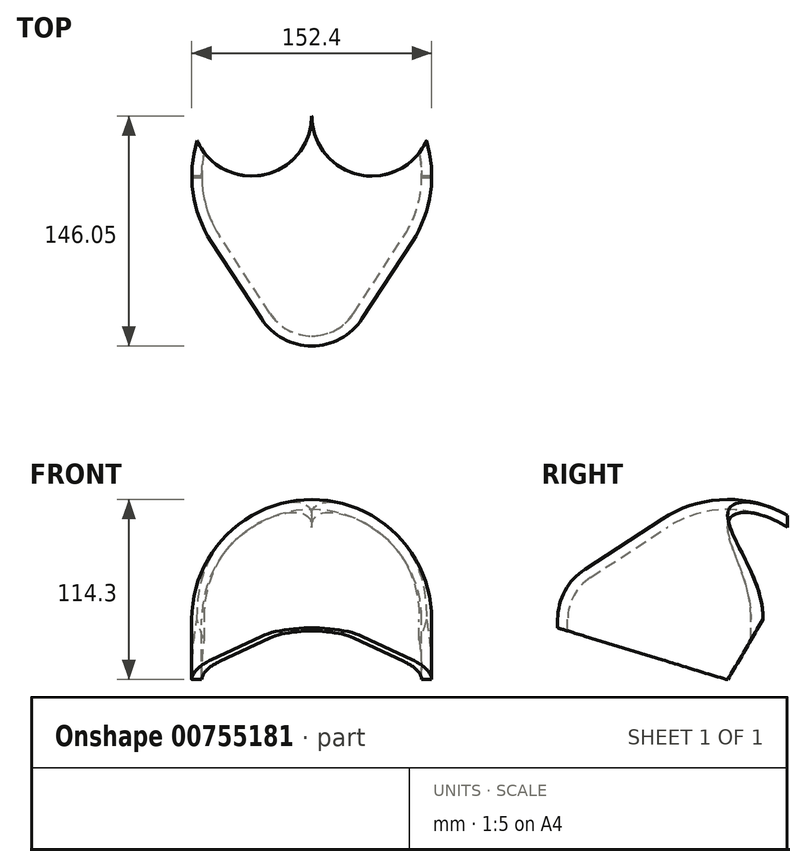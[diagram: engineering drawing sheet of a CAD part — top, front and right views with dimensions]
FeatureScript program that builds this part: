
annotation { "Feature Type Name" : "Feature", "Feature Type Description" : "" }
export const myFeature = defineFeature(function(context is Context, id is Id, definition is map)
    precondition{}
    {
        {
            var Q0;
            Q0=qCreatedBy(makeId("Top.planeOp"),FACE);
            var sketch = newSketch(context, id + "F0", { "sketchPlane" : qUnion([Q0])});
            skLineSegment(sketch, "E0", {"start": v(0, 76.2) * mm, "end": v(0, -101.6) * mm, "construction": true});
            skLineSegment(sketch, "E1", {"start": v(26.61, -87.17) * mm, "end": v(58.54, -38.1) * mm});
            skArc(sketch, "E2.trimOffspring", {"start": v(58.54, -38.1) * mm, "mid": v(61.4, 33.3) * mm, "end": v(0, 69.85) * mm});
            skArc(sketch, "E3.trimOffspring", {"start": v(0, -101.6) * mm, "mid": v(15.14, -97.76) * mm, "end": v(26.61, -87.17) * mm});
            skArc(sketch, "E4.0", {"start": v(63.87, -41.56) * mm, "mid": v(66.98, 36.33) * mm, "end": v(0, 76.2) * mm});
            skLineSegment(sketch, "E4.1", {"start": v(31.93, -90.63) * mm, "end": v(63.87, -41.56) * mm});
            skArc(sketch, "E4.2", {"start": v(0, -107.95) * mm, "mid": v(18.16, -103.34) * mm, "end": v(31.93, -90.63) * mm});
            skLineSegment(sketch, "E5", {"start": v(0, 69.85) * mm, "end": v(0, 76.2) * mm});
            skLineSegment(sketch, "E6", {"start": v(0, -107.95) * mm, "end": v(0, -101.6) * mm});
            skLineSegment(sketch, "E7", {"start": v(-72.03, 0) * mm, "end": v(69.85, 0) * mm, "construction": true});
            skArc(sketch, "E8", {"start": v(0, 38.1) * mm, "mid": v(65.04, 11.16) * mm, "end": v(38.1, 76.2) * mm});
            skArc(sketch, "E9", {"start": v(-38.1, 76.2) * mm, "mid": v(-65.04, 11.16) * mm, "end": v(0, 38.1) * mm});
            skArc(sketch, "E10.trimOffspring", {"start": v(38.1, 76.2) * mm, "mid": v(0, 114.3) * mm, "end": v(-38.1, 76.2) * mm});
            skSolve(sketch);
        }
        {
            var Q0;
            {var subQ0=sQuery(id+"F0.wireOp",EDGE,"E8");var subQ1=sQuery(id+"F0.wireOp",EDGE,"E2.trimOffspring");var subQ2=makeQuery(id+"F0.imprint","INTERSECT",VERTEX,{"disambiguationData":[OD(0.0)],"derivedFrom":[subQ1,subQ0]});Q0=makeQuery(id+"F0.imprint","IMPRINT",FACE,{"disambiguationData":[TD([[makeQuery(id+"F0.imprint","IMPRINT",EDGE,{"disambiguationData":[TD([[subQ2,-1.0]])],"derivedFrom":subQ1}),-1.0]])]});}
            var Q1;
            {var subQ5=sQuery(id+"F0.wireOp",EDGE,"E1");Q1=makeQuery(id+"F0.imprint","IMPRINT",FACE,{"disambiguationData":[TD([[makeQuery(id+"F0.imprint","IMPRINT",EDGE,{"derivedFrom":subQ5}),-1.0]])]});}
            var Q2;
            Q2=sQuery(id+"F0.wireOp",EDGE,"E0");
            revolve(context, id + "F1", {"surfaceOperationType" : NewSurfaceOperationType.NEW, "entities" : qUnion([Q0, Q1]), "axis" : qUnion([Q2]), "revolveType" : RevolveType.ONE_DIRECTION, "angle" : 180 * degree});
        }
        {
            var Q0;
            {var subQ0=sQuery(id+"F0.wireOp",EDGE,"E8");var subQ1=sQuery(id+"F0.wireOp",EDGE,"E4.0");var subQ2=makeQuery(id+"F0.imprint","INTERSECT",VERTEX,{"disambiguationData":[OD(0.0)],"derivedFrom":[subQ1,subQ0]});Q0=makeQuery(id+"F0.imprint","IMPRINT",FACE,{"disambiguationData":[TD([[makeQuery(id+"F0.imprint","IMPRINT",EDGE,{"disambiguationData":[TD([[subQ2,-1.0]])],"derivedFrom":subQ1}),-1.0]])]});}
            var Q1;
            {var subQ0=sQuery(id+"F0.wireOp",EDGE,"E8");var subQ1=sQuery(id+"F0.wireOp",EDGE,"E2.trimOffspring");var subQ2=makeQuery(id+"F0.imprint","INTERSECT",VERTEX,{"disambiguationData":[OD(0.0)],"derivedFrom":[subQ1,subQ0]});Q1=makeQuery(id+"F0.imprint","IMPRINT",FACE,{"disambiguationData":[TD([[makeQuery(id+"F0.imprint","IMPRINT",EDGE,{"disambiguationData":[TD([[subQ2,-1.0]])],"derivedFrom":subQ1}),-1.0]])]});}
            var Q2;
            {var subQ0=sQuery(id+"F0.wireOp",EDGE,"E8");var subQ1=sQuery(id+"F0.wireOp",EDGE,"E2.trimOffspring");var subQ2=makeQuery(id+"F0.imprint","INTERSECT",VERTEX,{"disambiguationData":[OD(0.0)],"derivedFrom":[subQ1,subQ0]});Q2=makeQuery(id+"F0.imprint","IMPRINT",FACE,{"disambiguationData":[TD([[makeQuery(id+"F0.imprint","IMPRINT",EDGE,{"disambiguationData":[TD([[subQ2,-1.0]])],"derivedFrom":subQ1}),1.0]])]});}
            var Q3;
            Q3=makeQuery(id+"F0.imprint","IMPRINT",FACE,{"disambiguationData":[TD([[makeQuery(id+"F0.imprint","IMPRINT",EDGE,{"derivedFrom":sQuery(id+"F0.wireOp",EDGE,"E9")}),1.0]])]});
            var Q4;
            {var subQ0=sQuery(id+"F0.wireOp",EDGE,"3955e8d2-0403-4676-987c-76ff6f28b55b");var subQ1=sQuery(id+"F0.wireOp",EDGE,"E2.trimOffspring");var subQ2=makeQuery(id+"F0.imprint","INTERSECT",VERTEX,{"derivedFrom":[subQ1,subQ0]});Q4=makeQuery(id+"F0.imprint","IMPRINT",FACE,{"disambiguationData":[TD([[makeQuery(id+"F0.imprint","IMPRINT",EDGE,{"disambiguationData":[TD([[subQ2,-1.0]])],"derivedFrom":subQ1}),-1.0]])]});}
            var Q5;
            {var subQ0=sQuery(id+"F0.wireOp",EDGE,"E5");Q5=makeQuery(id+"F0.imprint","IMPRINT",FACE,{"disambiguationData":[TD([[makeQuery(id+"F0.imprint","IMPRINT",EDGE,{"derivedFrom":subQ0}),1.0]])]});}
            extrude(context, id + "F2", {"entities" : qUnion([Q0, Q1, Q2, Q3, Q4, Q5]), "operationType" : NewBodyOperationType.REMOVE, "endBound" : BoundingType.THROUGH_ALL, "depth" : 25.4 * mm, "offsetDistance" : 25.4 * mm});
        }
        {
            var Q0;
            Q0=makeQuery(id+"F1.opRevolve","CAP_FACE",FACE,{"disambiguationData":[OSD([sQuery(id+"F0.wireOp",EDGE,"E1"),sQuery(id+"F0.wireOp",EDGE,"E2.trimOffspring"),sQuery(id+"F0.wireOp",EDGE,"E3.trimOffspring"),sQuery(id+"F0.wireOp",EDGE,"E4.0"),sQuery(id+"F0.wireOp",EDGE,"E4.1"),sQuery(id+"F0.wireOp",EDGE,"E4.2"),sQuery(id+"F0.wireOp",EDGE,"E5"),sQuery(id+"F0.wireOp",EDGE,"E6")])],"isStart":true});
            extrude(context, id + "F3", {"entities" : qUnion([Q0]), "operationType" : NewBodyOperationType.ADD, "depth" : 38.1 * mm, "offsetDistance" : 25.4 * mm});
        }
        {
            var Q0;
            Q0=qCreatedBy(makeId("Right.planeOp"),FACE);
            var sketch = newSketch(context, id + "F4", { "sketchPlane" : qUnion([Q0])});
            skLineSegment(sketch, "E11", {"start": v(111.37, 0) * mm, "end": v(-125.47, 0) * mm, "construction": true});
            skLineSegment(sketch, "E12", {"start": v(0, -74.76) * mm, "end": v(0, 139.83) * mm, "construction": true});
            skLineSegment(sketch, "E13", {"start": v(0, -38.4) * mm, "end": v(22.41, 0) * mm});
            skLineSegment(sketch, "E14", {"start": v(0, -38.4) * mm, "end": v(-125.47, 0) * mm});
            skLineSegment(sketch, "E15", {"start": v(-125.47, -38.4) * mm, "end": v(-125.47, 0) * mm});
            skLineSegment(sketch, "E16", {"start": v(0, -38.4) * mm, "end": v(-125.47, -38.4) * mm});
            skLineSegment(sketch, "E17", {"start": v(-2.29, -42.3) * mm, "end": v(29.73, 12.53) * mm});
            skLineSegment(sketch, "E18", {"start": v(29.73, 12.53) * mm, "end": v(29.73, -42.3) * mm});
            skLineSegment(sketch, "E19", {"start": v(29.73, -42.3) * mm, "end": v(-2.29, -42.3) * mm});
            skPoint(sketch, "E20.start.orphan", {"position": v(22.41, -38.4) * mm});
            skSolve(sketch);
        }
        {
            var Q0;
            {var subQ3=sQuery(id+"F4.wireOp",EDGE,"E18");Q0=makeQuery(id+"F4.imprint","IMPRINT",FACE,{"disambiguationData":[TD([[makeQuery(id+"F4.imprint","IMPRINT",EDGE,{"derivedFrom":subQ3}),-1.0]])]});}
            var Q1;
            Q1=makeQuery(id+"F4.imprint","IMPRINT",FACE,{"disambiguationData":[TD([[makeQuery(id+"F4.imprint","IMPRINT",EDGE,{"derivedFrom":sQuery(id+"F4.wireOp",EDGE,"E14")}),1.0]])]});
            extrude(context, id + "F5", {"entities" : qUnion([Q0, Q1]), "operationType" : NewBodyOperationType.REMOVE, "endBound" : BoundingType.SYMMETRIC, "oppositeDirection" : true, "depth" : 254 * mm, "offsetDistance" : 25.4 * mm});
        }
    });
